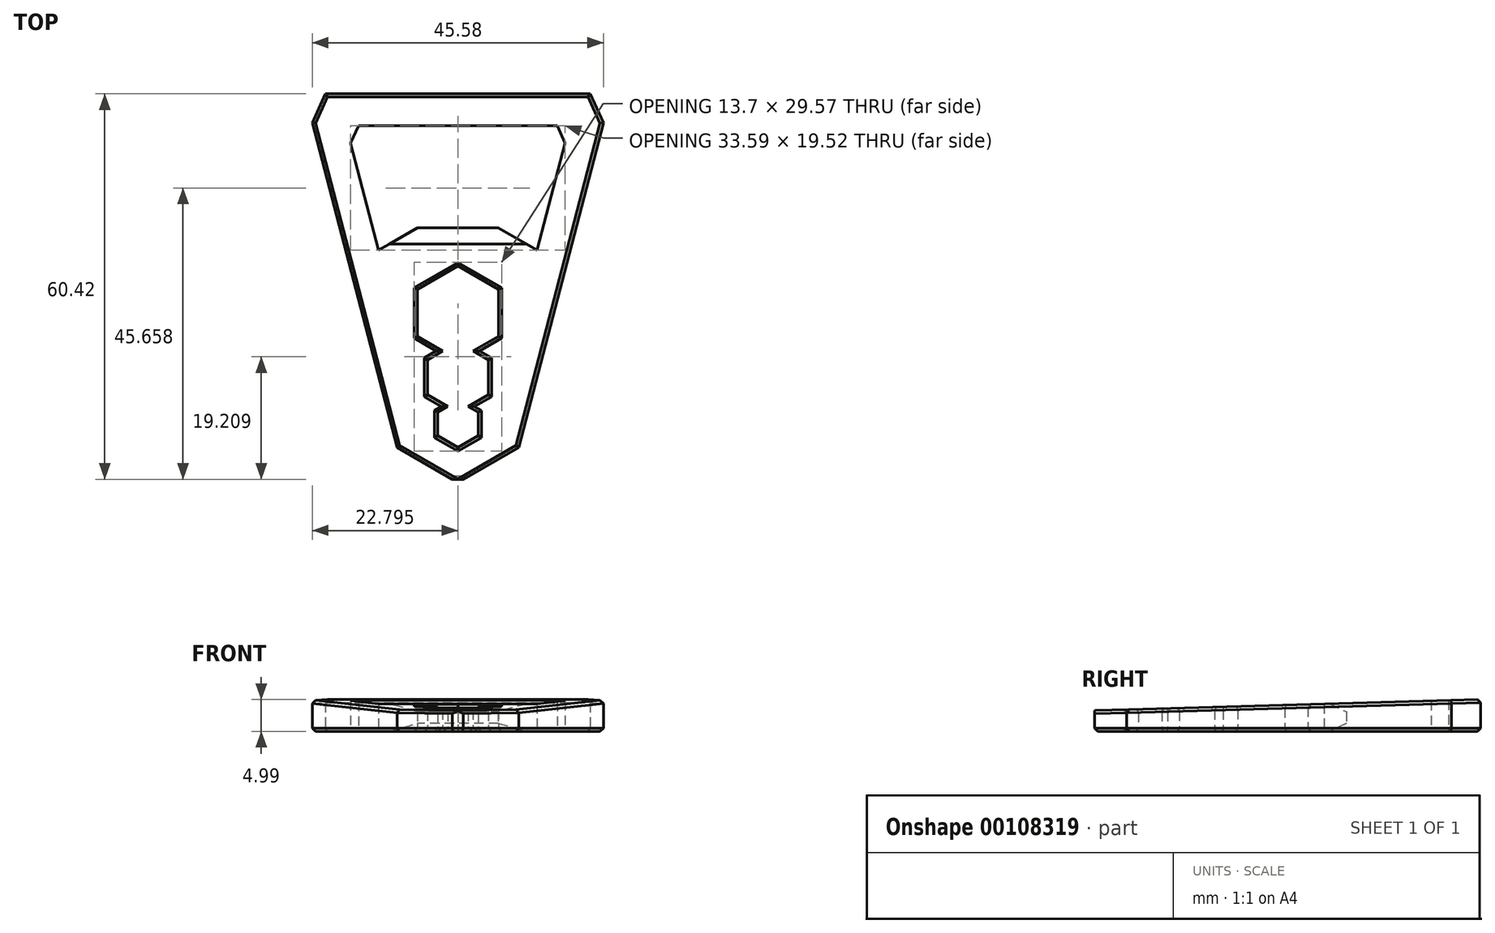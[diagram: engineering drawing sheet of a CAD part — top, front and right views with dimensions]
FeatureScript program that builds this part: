
annotation { "Feature Type Name" : "Feature", "Feature Type Description" : "" }
export const myFeature = defineFeature(function(context is Context, id is Id, definition is map)
    precondition{}
    {
        {
            var Q0;
            Q0=qCreatedBy(makeId("Top.planeOp"),FACE);
            var sketch = newSketch(context, id + "F0", { "sketchPlane" : qUnion([Q0])});
            skLineSegment(sketch, "E0", {"start": v(-34.12, -3.9) * mm, "end": v(-47.38, 46.95) * mm});
            skLineSegment(sketch, "E1", {"start": v(-47.38, 46.95) * mm, "end": v(-45.33, 51.5) * mm});
            skLineSegment(sketch, "E2", {"start": v(-45.33, 51.5) * mm, "end": v(-3.84, 51.5) * mm});
            skLineSegment(sketch, "E3", {"start": v(-3.84, 51.5) * mm, "end": v(-1.8, 46.95) * mm});
            skLineSegment(sketch, "E4", {"start": v(-1.8, 46.95) * mm, "end": v(-15.05, -3.9) * mm});
            skLineSegment(sketch, "E5", {"start": v(-23.71, -8.9) * mm, "end": v(-25.46, -8.9) * mm});
            skLineSegment(sketch, "E6", {"start": v(-24.59, -8.9) * mm, "end": v(-24.59, 51.5) * mm, "construction": true});
            skLineSegment(sketch, "E7", {"start": v(-15.05, -3.9) * mm, "end": v(-34.12, -3.9) * mm, "construction": true});
            skLineSegment(sketch, "E8", {"start": v(-1.8, 46.95) * mm, "end": v(-47.38, 46.95) * mm, "construction": true});
            skPoint(sketch, "E9", {"position": v(-24.59, 46.95) * mm});
            skPoint(sketch, "E10", {"position": v(-24.59, -3.9) * mm});
            skCircle(sketch, "E11.cCircle", {"center": v(-24.59, -0.24) * mm, "radius": 3.18 * mm, "construction": true});
            skLineSegment(sketch, "E11.0", {"start": v(-24.59, 3.43) * mm, "end": v(-21.41, 1.6) * mm, "construction": true});
            skLineSegment(sketch, "E11.1", {"start": v(-21.41, 1.6) * mm, "end": v(-21.41, -2.07) * mm, "construction": true});
            skLineSegment(sketch, "E11.2", {"start": v(-21.41, -2.07) * mm, "end": v(-24.59, -3.9) * mm, "construction": true});
            skLineSegment(sketch, "E11.3", {"start": v(-24.59, -3.9) * mm, "end": v(-27.76, -2.07) * mm, "construction": true});
            skLineSegment(sketch, "E11.4", {"start": v(-27.76, -2.07) * mm, "end": v(-27.76, 1.6) * mm, "construction": true});
            skLineSegment(sketch, "E11.5", {"start": v(-27.76, 1.6) * mm, "end": v(-24.59, 3.43) * mm, "construction": true});
            skPoint(sketch, "E11.0.midPoint", {"position": v(-23, 2.5) * mm});
            skCircle(sketch, "E12.cCircle", {"center": v(-24.59, 7.1) * mm, "radius": 4.76 * mm, "construction": true});
            skLineSegment(sketch, "E12.0", {"start": v(-29.35, 4.34) * mm, "end": v(-29.35, 9.84) * mm, "construction": true});
            skLineSegment(sketch, "E12.1", {"start": v(-29.35, 9.84) * mm, "end": v(-24.59, 12.6) * mm, "construction": true});
            skLineSegment(sketch, "E12.2", {"start": v(-24.59, 12.6) * mm, "end": v(-19.82, 9.84) * mm, "construction": true});
            skLineSegment(sketch, "E12.3", {"start": v(-19.82, 9.84) * mm, "end": v(-19.82, 4.34) * mm, "construction": true});
            skLineSegment(sketch, "E12.4", {"start": v(-19.82, 4.34) * mm, "end": v(-24.59, 1.6) * mm, "construction": true});
            skLineSegment(sketch, "E12.5", {"start": v(-24.59, 1.6) * mm, "end": v(-29.35, 4.34) * mm, "construction": true});
            skPoint(sketch, "E12.0.midPoint", {"position": v(-29.35, 7.1) * mm});
            skCircle(sketch, "E13.cCircle", {"center": v(-24.59, 17.17) * mm, "radius": 6.35 * mm, "construction": true});
            skLineSegment(sketch, "E13.0", {"start": v(-30.94, 13.5) * mm, "end": v(-30.94, 20.84) * mm, "construction": true});
            skLineSegment(sketch, "E13.1", {"start": v(-30.94, 20.84) * mm, "end": v(-24.59, 24.5) * mm, "construction": true});
            skLineSegment(sketch, "E13.2", {"start": v(-24.59, 24.5) * mm, "end": v(-18.24, 20.84) * mm, "construction": true});
            skLineSegment(sketch, "E13.3", {"start": v(-18.24, 20.84) * mm, "end": v(-18.24, 13.5) * mm, "construction": true});
            skLineSegment(sketch, "E13.4", {"start": v(-18.24, 13.5) * mm, "end": v(-24.59, 9.84) * mm, "construction": true});
            skLineSegment(sketch, "E13.5", {"start": v(-24.59, 9.84) * mm, "end": v(-30.94, 13.5) * mm, "construction": true});
            skPoint(sketch, "E13.0.midPoint", {"position": v(-30.94, 17.17) * mm});
            skLineSegment(sketch, "E14", {"start": v(-38.21, 43.5) * mm, "end": v(-10.96, 43.5) * mm, "construction": true});
            skLineSegment(sketch, "E15", {"start": v(-10.96, 43.5) * mm, "end": v(-13.57, 33.5) * mm, "construction": true});
            skLineSegment(sketch, "E16", {"start": v(-13.57, 33.5) * mm, "end": v(-35.6, 33.5) * mm, "construction": true});
            skLineSegment(sketch, "E17", {"start": v(-35.6, 33.5) * mm, "end": v(-38.21, 43.5) * mm, "construction": true});
            skPoint(sketch, "E18", {"position": v(-24.59, 43.5) * mm});
            skPoint(sketch, "E19", {"position": v(-24.59, 33.5) * mm});
            skLineSegment(sketch, "E20", {"start": v(-42.1, 46.5) * mm, "end": v(-7.08, 46.5) * mm, "construction": true});
            skLineSegment(sketch, "E21", {"start": v(-7.08, 46.5) * mm, "end": v(-11.25, 30.5) * mm, "construction": true});
            skLineSegment(sketch, "E22", {"start": v(-18.25, 30.5) * mm, "end": v(-30.92, 30.5) * mm, "construction": true});
            skLineSegment(sketch, "E23", {"start": v(-37.92, 30.5) * mm, "end": v(-42.1, 46.5) * mm, "construction": true});
            skLineSegment(sketch, "E24", {"start": v(-36.9, 38.5) * mm, "end": v(-39.81, 37.75) * mm, "construction": true});
            skLineSegment(sketch, "E25", {"start": v(-12.26, 38.5) * mm, "end": v(-9.36, 37.75) * mm, "construction": true});
            skLineSegment(sketch, "E26", {"start": v(-24.59, 46.5) * mm, "end": v(-24.59, 43.5) * mm, "construction": true});
            skLineSegment(sketch, "E27", {"start": v(-24.59, 33.5) * mm, "end": v(-24.59, 30.5) * mm, "construction": true});
            skLineSegment(sketch, "E28", {"start": v(-7.08, 46.5) * mm, "end": v(-7.08, 51.5) * mm, "construction": true});
            skLineSegment(sketch, "E29", {"start": v(-7.08, 46.5) * mm, "end": v(-2.24, 45.24) * mm, "construction": true});
            skPoint(sketch, "E30", {"position": v(-22.2, 11.22) * mm});
            skLineSegment(sketch, "E31", {"start": v(-30.92, 30.5) * mm, "end": v(-37, 26.99) * mm, "construction": true});
            skLineSegment(sketch, "E32", {"start": v(-18.25, 30.5) * mm, "end": v(-12.16, 26.99) * mm, "construction": true});
            skLineSegment(sketch, "E33", {"start": v(-37.92, 30.5) * mm, "end": v(-37, 26.99) * mm, "construction": true});
            skLineSegment(sketch, "E34", {"start": v(-11.25, 30.5) * mm, "end": v(-12.16, 26.99) * mm, "construction": true});
            skLineSegment(sketch, "E35", {"start": v(-7.08, 46.5) * mm, "end": v(-2.52, 48.56) * mm, "construction": true});
            skLineSegment(sketch, "E36", {"start": v(-15.05, -3.9) * mm, "end": v(-23.71, -8.9) * mm});
            skLineSegment(sketch, "E37", {"start": v(-25.46, -8.9) * mm, "end": v(-34.12, -3.9) * mm});
            skLineSegment(sketch, "E38", {"start": v(-24.59, -3.9) * mm, "end": v(-21.41, -2.07) * mm});
            skLineSegment(sketch, "E39", {"start": v(-21.41, 1.6) * mm, "end": v(-23, 2.5) * mm});
            skLineSegment(sketch, "E40", {"start": v(-19.82, 4.34) * mm, "end": v(-19.82, 9.84) * mm});
            skLineSegment(sketch, "E41", {"start": v(-22.2, 11.22) * mm, "end": v(-18.24, 13.5) * mm});
            skLineSegment(sketch, "E42", {"start": v(-18.24, 20.84) * mm, "end": v(-24.59, 24.5) * mm});
            skLineSegment(sketch, "E43", {"start": v(-30.94, 20.84) * mm, "end": v(-30.94, 13.5) * mm});
            skLineSegment(sketch, "E44", {"start": v(-26.97, 11.22) * mm, "end": v(-29.35, 9.84) * mm});
            skLineSegment(sketch, "E45", {"start": v(-29.35, 4.34) * mm, "end": v(-26.17, 2.5) * mm});
            skLineSegment(sketch, "E46", {"start": v(-26.17, 2.5) * mm, "end": v(-27.76, 1.6) * mm});
            skLineSegment(sketch, "E47", {"start": v(-27.76, -2.07) * mm, "end": v(-24.59, -3.9) * mm});
            skLineSegment(sketch, "E48", {"start": v(-30.94, 20.84) * mm, "end": v(-24.59, 24.5) * mm});
            skLineSegment(sketch, "E49", {"start": v(-18.24, 13.5) * mm, "end": v(-18.24, 20.84) * mm});
            skLineSegment(sketch, "E50", {"start": v(-21.41, -2.07) * mm, "end": v(-21.41, 1.6) * mm});
            skLineSegment(sketch, "E51", {"start": v(-19.82, 4.34) * mm, "end": v(-23, 2.5) * mm});
            skLineSegment(sketch, "E52", {"start": v(-22.2, 11.22) * mm, "end": v(-19.82, 9.84) * mm});
            skLineSegment(sketch, "E53", {"start": v(-30.94, 13.5) * mm, "end": v(-26.97, 11.22) * mm});
            skLineSegment(sketch, "E54", {"start": v(-29.35, 9.84) * mm, "end": v(-29.35, 4.34) * mm});
            skLineSegment(sketch, "E55", {"start": v(-27.76, 1.6) * mm, "end": v(-27.76, -2.07) * mm});
            skLineSegment(sketch, "E56", {"start": v(-41.38, 43.77) * mm, "end": v(-40.15, 46.5) * mm});
            skLineSegment(sketch, "E57", {"start": v(-40.15, 46.5) * mm, "end": v(-9.02, 46.5) * mm});
            skLineSegment(sketch, "E58", {"start": v(-9.02, 46.5) * mm, "end": v(-7.8, 43.77) * mm});
            skLineSegment(sketch, "E59", {"start": v(-7.8, 43.77) * mm, "end": v(-12.16, 26.99) * mm});
            skLineSegment(sketch, "E60", {"start": v(-18.25, 30.5) * mm, "end": v(-30.92, 30.5) * mm});
            skLineSegment(sketch, "E61", {"start": v(-18.25, 30.5) * mm, "end": v(-12.16, 26.99) * mm});
            skLineSegment(sketch, "E62", {"start": v(-30.92, 30.5) * mm, "end": v(-37, 26.99) * mm});
            skLineSegment(sketch, "E63", {"start": v(-37, 26.99) * mm, "end": v(-41.38, 43.77) * mm});
            skLineSegment(sketch, "E64", {"start": v(-8.22, 44.74) * mm, "end": v(-10.96, 43.5) * mm, "construction": true});
            skLineSegment(sketch, "E65", {"start": v(-24.59, -3.9) * mm, "end": v(-24.59, -8.9) * mm});
            skSolve(sketch);
        }
        {
            var Q0;
            Q0 = qSketchRegion(id + "F0", true);
            extrude(context, id + "F1", {"entities" : qUnion([Q0]), "depth" : 5 * mm});
        }
        {
            var Q0;
            Q0=qCreatedBy(makeId("Right.planeOp"),FACE);
            var sketch = newSketch(context, id + "F2", { "sketchPlane" : qUnion([Q0])});
            skLineSegment(sketch, "E66", {"start": v(-8.9, 3.25) * mm, "end": v(51.5, 5) * mm});
            skLineSegment(sketch, "E67", {"start": v(-8.9, 3.25) * mm, "end": v(-8.9, 5) * mm});
            skLineSegment(sketch, "E68", {"start": v(-8.9, 5) * mm, "end": v(51.5, 5) * mm});
            skSolve(sketch);
        }
        {
            var Q0;
            Q0 = qSketchRegion(id + "F2", true);
            extrude(context, id + "F3", {"entities" : qUnion([Q0]), "operationType" : NewBodyOperationType.REMOVE, "endBound" : BoundingType.THROUGH_ALL, "oppositeDirection" : true, "depth" : 25 * mm});
        }
        {
            var Q0;
            Q0=makeQuery(id+"F1.opExtrude","CAP_EDGE",EDGE,{"disambiguationData":[OSD([sQuery(id+"F0.wireOp",EDGE,"E60")])],"isStart":false});
            var Q1;
            Q1=makeQuery(id+"F1.opExtrude","CAP_EDGE",EDGE,{"disambiguationData":[OSD([sQuery(id+"F0.wireOp",EDGE,"E60")])],"isStart":true});
            var Q2;
            Q2=makeQuery(id+"F3.boolean.opBoolean","INTERSECT",EDGE,{"derivedFrom":[makeQuery(id+"F1.opExtrude","SWEPT_FACE",FACE,{"disambiguationData":[OSD([sQuery(id+"F0.wireOp",EDGE,"E60")])]}),makeQuery(id+"F3.opExtrude","SWEPT_FACE",FACE,{"disambiguationData":[OSD([sQuery(id+"F2.wireOp",EDGE,"E66")])]})]});
            chamfer(context, id + "F4", {"entities" : qUnion([Q0, Q1, Q2]), "chamferType" : ChamferType.TWO_OFFSETS, "width1" : 1.25 * mm, "oppositeDirection" : false, "width2" : 2.5 * mm});
        }
        {
            var Q0;
            Q0=makeQuery(id+"F3.boolean.opBoolean","MERGE",EDGE,{"derivedFrom":[makeQuery(id+"F1.opExtrude","CAP_EDGE",EDGE,{"disambiguationData":[OSD([sQuery(id+"F0.wireOp",EDGE,"E2")])],"isStart":false}),makeQuery(id+"F3.opExtrude","SWEPT_EDGE",EDGE,{"disambiguationData":[OSD([sQuery(id+"F2.wireOp",EDGE,"E66"),sQuery(id+"F2.wireOp",EDGE,"E68")])]})]});
            var Q1;
            Q1=makeQuery(id+"F3.boolean.opBoolean","INTERSECT",EDGE,{"derivedFrom":[makeQuery(id+"F1.opExtrude","SWEPT_FACE",FACE,{"disambiguationData":[OSD([sQuery(id+"F0.wireOp",EDGE,"E1")])]}),makeQuery(id+"F3.opExtrude","SWEPT_FACE",FACE,{"disambiguationData":[OSD([sQuery(id+"F2.wireOp",EDGE,"E66")])]})]});
            var Q2;
            Q2=makeQuery(id+"F1.opExtrude","CAP_EDGE",EDGE,{"disambiguationData":[OSD([sQuery(id+"F0.wireOp",EDGE,"E1")])],"isStart":true});
            var Q3;
            Q3=makeQuery(id+"F1.opExtrude","CAP_EDGE",EDGE,{"disambiguationData":[OSD([sQuery(id+"F0.wireOp",EDGE,"E2")])],"isStart":true});
            var Q4;
            Q4=makeQuery(id+"F1.opExtrude","CAP_EDGE",EDGE,{"disambiguationData":[OSD([sQuery(id+"F0.wireOp",EDGE,"E3")])],"isStart":true});
            var Q5;
            Q5=makeQuery(id+"F3.boolean.opBoolean","INTERSECT",EDGE,{"derivedFrom":[makeQuery(id+"F1.opExtrude","SWEPT_FACE",FACE,{"disambiguationData":[OSD([sQuery(id+"F0.wireOp",EDGE,"E3")])]}),makeQuery(id+"F3.opExtrude","SWEPT_FACE",FACE,{"disambiguationData":[OSD([sQuery(id+"F2.wireOp",EDGE,"E66")])]})]});
            var Q6;
            Q6=makeQuery(id+"F3.boolean.opBoolean","INTERSECT",EDGE,{"derivedFrom":[makeQuery(id+"F1.opExtrude","SWEPT_FACE",FACE,{"disambiguationData":[OSD([sQuery(id+"F0.wireOp",EDGE,"E4")])]}),makeQuery(id+"F3.opExtrude","SWEPT_FACE",FACE,{"disambiguationData":[OSD([sQuery(id+"F2.wireOp",EDGE,"E66")])]})]});
            var Q7;
            Q7=makeQuery(id+"F1.opExtrude","CAP_EDGE",EDGE,{"disambiguationData":[OSD([sQuery(id+"F0.wireOp",EDGE,"E4")])],"isStart":true});
            var Q8;
            Q8=makeQuery(id+"F3.boolean.opBoolean","INTERSECT",EDGE,{"derivedFrom":[makeQuery(id+"F1.opExtrude","SWEPT_FACE",FACE,{"disambiguationData":[OSD([sQuery(id+"F0.wireOp",EDGE,"E36")])]}),makeQuery(id+"F3.opExtrude","SWEPT_FACE",FACE,{"disambiguationData":[OSD([sQuery(id+"F2.wireOp",EDGE,"E66")])]})]});
            var Q9;
            Q9=makeQuery(id+"F1.opExtrude","CAP_EDGE",EDGE,{"disambiguationData":[OSD([sQuery(id+"F0.wireOp",EDGE,"E36")])],"isStart":true});
            var Q10;
            Q10=makeQuery(id+"F3.boolean.opBoolean","COPY",EDGE,{"derivedFrom":makeQuery(id+"F3.opExtrude","SWEPT_EDGE",EDGE,{"disambiguationData":[OSD([sQuery(id+"F2.wireOp",EDGE,"E66"),sQuery(id+"F2.wireOp",EDGE,"E67")])]})});
            var Q11;
            Q11=makeQuery(id+"F1.opExtrude","CAP_EDGE",EDGE,{"disambiguationData":[OSD([sQuery(id+"F0.wireOp",EDGE,"E5")])],"isStart":true});
            var Q12;
            Q12=makeQuery(id+"F1.opExtrude","CAP_EDGE",EDGE,{"disambiguationData":[OSD([sQuery(id+"F0.wireOp",EDGE,"E37")])],"isStart":true});
            var Q13;
            Q13=makeQuery(id+"F3.boolean.opBoolean","INTERSECT",EDGE,{"derivedFrom":[makeQuery(id+"F1.opExtrude","SWEPT_FACE",FACE,{"disambiguationData":[OSD([sQuery(id+"F0.wireOp",EDGE,"E37")])]}),makeQuery(id+"F3.opExtrude","SWEPT_FACE",FACE,{"disambiguationData":[OSD([sQuery(id+"F2.wireOp",EDGE,"E66")])]})]});
            var Q14;
            Q14=makeQuery(id+"F3.boolean.opBoolean","INTERSECT",EDGE,{"derivedFrom":[makeQuery(id+"F1.opExtrude","SWEPT_FACE",FACE,{"disambiguationData":[OSD([sQuery(id+"F0.wireOp",EDGE,"E0")])]}),makeQuery(id+"F3.opExtrude","SWEPT_FACE",FACE,{"disambiguationData":[OSD([sQuery(id+"F2.wireOp",EDGE,"E66")])]})]});
            var Q15;
            Q15=makeQuery(id+"F1.opExtrude","CAP_EDGE",EDGE,{"disambiguationData":[OSD([sQuery(id+"F0.wireOp",EDGE,"E0")])],"isStart":true});
            var Q16;
            Q16=makeQuery(id+"F3.boolean.opBoolean","INTERSECT",EDGE,{"derivedFrom":[makeQuery(id+"F1.opExtrude","SWEPT_FACE",FACE,{"disambiguationData":[OSD([sQuery(id+"F0.wireOp",EDGE,"E49")])]}),makeQuery(id+"F3.opExtrude","SWEPT_FACE",FACE,{"disambiguationData":[OSD([sQuery(id+"F2.wireOp",EDGE,"E66")])]})]});
            var Q17;
            Q17=makeQuery(id+"F3.boolean.opBoolean","INTERSECT",EDGE,{"derivedFrom":[makeQuery(id+"F1.opExtrude","SWEPT_FACE",FACE,{"disambiguationData":[OSD([sQuery(id+"F0.wireOp",EDGE,"E42")])]}),makeQuery(id+"F3.opExtrude","SWEPT_FACE",FACE,{"disambiguationData":[OSD([sQuery(id+"F2.wireOp",EDGE,"E66")])]})]});
            var Q18;
            Q18=makeQuery(id+"F3.boolean.opBoolean","INTERSECT",EDGE,{"derivedFrom":[makeQuery(id+"F1.opExtrude","SWEPT_FACE",FACE,{"disambiguationData":[OSD([sQuery(id+"F0.wireOp",EDGE,"E48")])]}),makeQuery(id+"F3.opExtrude","SWEPT_FACE",FACE,{"disambiguationData":[OSD([sQuery(id+"F2.wireOp",EDGE,"E66")])]})]});
            var Q19;
            Q19=makeQuery(id+"F3.boolean.opBoolean","INTERSECT",EDGE,{"derivedFrom":[makeQuery(id+"F1.opExtrude","SWEPT_FACE",FACE,{"disambiguationData":[OSD([sQuery(id+"F0.wireOp",EDGE,"E43")])]}),makeQuery(id+"F3.opExtrude","SWEPT_FACE",FACE,{"disambiguationData":[OSD([sQuery(id+"F2.wireOp",EDGE,"E66")])]})]});
            var Q20;
            Q20=makeQuery(id+"F3.boolean.opBoolean","INTERSECT",EDGE,{"derivedFrom":[makeQuery(id+"F1.opExtrude","SWEPT_FACE",FACE,{"disambiguationData":[OSD([sQuery(id+"F0.wireOp",EDGE,"E53")])]}),makeQuery(id+"F3.opExtrude","SWEPT_FACE",FACE,{"disambiguationData":[OSD([sQuery(id+"F2.wireOp",EDGE,"E66")])]})]});
            var Q21;
            Q21=makeQuery(id+"F3.boolean.opBoolean","INTERSECT",EDGE,{"derivedFrom":[makeQuery(id+"F1.opExtrude","SWEPT_FACE",FACE,{"disambiguationData":[OSD([sQuery(id+"F0.wireOp",EDGE,"E41")])]}),makeQuery(id+"F3.opExtrude","SWEPT_FACE",FACE,{"disambiguationData":[OSD([sQuery(id+"F2.wireOp",EDGE,"E66")])]})]});
            var Q22;
            Q22=makeQuery(id+"F3.boolean.opBoolean","INTERSECT",EDGE,{"derivedFrom":[makeQuery(id+"F1.opExtrude","SWEPT_FACE",FACE,{"disambiguationData":[OSD([sQuery(id+"F0.wireOp",EDGE,"E52")])]}),makeQuery(id+"F3.opExtrude","SWEPT_FACE",FACE,{"disambiguationData":[OSD([sQuery(id+"F2.wireOp",EDGE,"E66")])]})]});
            var Q23;
            Q23=makeQuery(id+"F3.boolean.opBoolean","INTERSECT",EDGE,{"derivedFrom":[makeQuery(id+"F1.opExtrude","SWEPT_FACE",FACE,{"disambiguationData":[OSD([sQuery(id+"F0.wireOp",EDGE,"E40")])]}),makeQuery(id+"F3.opExtrude","SWEPT_FACE",FACE,{"disambiguationData":[OSD([sQuery(id+"F2.wireOp",EDGE,"E66")])]})]});
            var Q24;
            Q24=makeQuery(id+"F3.boolean.opBoolean","INTERSECT",EDGE,{"derivedFrom":[makeQuery(id+"F1.opExtrude","SWEPT_FACE",FACE,{"disambiguationData":[OSD([sQuery(id+"F0.wireOp",EDGE,"E51")])]}),makeQuery(id+"F3.opExtrude","SWEPT_FACE",FACE,{"disambiguationData":[OSD([sQuery(id+"F2.wireOp",EDGE,"E66")])]})]});
            var Q25;
            Q25=makeQuery(id+"F3.boolean.opBoolean","INTERSECT",EDGE,{"derivedFrom":[makeQuery(id+"F1.opExtrude","SWEPT_FACE",FACE,{"disambiguationData":[OSD([sQuery(id+"F0.wireOp",EDGE,"E39")])]}),makeQuery(id+"F3.opExtrude","SWEPT_FACE",FACE,{"disambiguationData":[OSD([sQuery(id+"F2.wireOp",EDGE,"E66")])]})]});
            var Q26;
            Q26=makeQuery(id+"F3.boolean.opBoolean","INTERSECT",EDGE,{"derivedFrom":[makeQuery(id+"F1.opExtrude","SWEPT_FACE",FACE,{"disambiguationData":[OSD([sQuery(id+"F0.wireOp",EDGE,"E50")])]}),makeQuery(id+"F3.opExtrude","SWEPT_FACE",FACE,{"disambiguationData":[OSD([sQuery(id+"F2.wireOp",EDGE,"E66")])]})]});
            var Q27;
            Q27=makeQuery(id+"F3.boolean.opBoolean","INTERSECT",EDGE,{"derivedFrom":[makeQuery(id+"F1.opExtrude","SWEPT_FACE",FACE,{"disambiguationData":[OSD([sQuery(id+"F0.wireOp",EDGE,"E38")])]}),makeQuery(id+"F3.opExtrude","SWEPT_FACE",FACE,{"disambiguationData":[OSD([sQuery(id+"F2.wireOp",EDGE,"E66")])]})]});
            var Q28;
            Q28=makeQuery(id+"F3.boolean.opBoolean","INTERSECT",EDGE,{"derivedFrom":[makeQuery(id+"F1.opExtrude","SWEPT_FACE",FACE,{"disambiguationData":[OSD([sQuery(id+"F0.wireOp",EDGE,"E47")])]}),makeQuery(id+"F3.opExtrude","SWEPT_FACE",FACE,{"disambiguationData":[OSD([sQuery(id+"F2.wireOp",EDGE,"E66")])]})]});
            var Q29;
            Q29=makeQuery(id+"F3.boolean.opBoolean","INTERSECT",EDGE,{"derivedFrom":[makeQuery(id+"F1.opExtrude","SWEPT_FACE",FACE,{"disambiguationData":[OSD([sQuery(id+"F0.wireOp",EDGE,"E55")])]}),makeQuery(id+"F3.opExtrude","SWEPT_FACE",FACE,{"disambiguationData":[OSD([sQuery(id+"F2.wireOp",EDGE,"E66")])]})]});
            var Q30;
            Q30=makeQuery(id+"F3.boolean.opBoolean","INTERSECT",EDGE,{"derivedFrom":[makeQuery(id+"F1.opExtrude","SWEPT_FACE",FACE,{"disambiguationData":[OSD([sQuery(id+"F0.wireOp",EDGE,"E46")])]}),makeQuery(id+"F3.opExtrude","SWEPT_FACE",FACE,{"disambiguationData":[OSD([sQuery(id+"F2.wireOp",EDGE,"E66")])]})]});
            var Q31;
            Q31=makeQuery(id+"F3.boolean.opBoolean","INTERSECT",EDGE,{"derivedFrom":[makeQuery(id+"F1.opExtrude","SWEPT_FACE",FACE,{"disambiguationData":[OSD([sQuery(id+"F0.wireOp",EDGE,"E45")])]}),makeQuery(id+"F3.opExtrude","SWEPT_FACE",FACE,{"disambiguationData":[OSD([sQuery(id+"F2.wireOp",EDGE,"E66")])]})]});
            var Q32;
            Q32=makeQuery(id+"F3.boolean.opBoolean","INTERSECT",EDGE,{"derivedFrom":[makeQuery(id+"F1.opExtrude","SWEPT_FACE",FACE,{"disambiguationData":[OSD([sQuery(id+"F0.wireOp",EDGE,"E54")])]}),makeQuery(id+"F3.opExtrude","SWEPT_FACE",FACE,{"disambiguationData":[OSD([sQuery(id+"F2.wireOp",EDGE,"E66")])]})]});
            var Q33;
            Q33=makeQuery(id+"F3.boolean.opBoolean","INTERSECT",EDGE,{"derivedFrom":[makeQuery(id+"F1.opExtrude","SWEPT_FACE",FACE,{"disambiguationData":[OSD([sQuery(id+"F0.wireOp",EDGE,"E44")])]}),makeQuery(id+"F3.opExtrude","SWEPT_FACE",FACE,{"disambiguationData":[OSD([sQuery(id+"F2.wireOp",EDGE,"E66")])]})]});
            var Q34;
            Q34=makeQuery(id+"F1.opExtrude","CAP_EDGE",EDGE,{"disambiguationData":[OSD([sQuery(id+"F0.wireOp",EDGE,"E55")])],"isStart":true});
            var Q35;
            Q35=makeQuery(id+"F1.opExtrude","CAP_EDGE",EDGE,{"disambiguationData":[OSD([sQuery(id+"F0.wireOp",EDGE,"E47")])],"isStart":true});
            var Q36;
            Q36=makeQuery(id+"F1.opExtrude","CAP_EDGE",EDGE,{"disambiguationData":[OSD([sQuery(id+"F0.wireOp",EDGE,"E38")])],"isStart":true});
            var Q37;
            Q37=makeQuery(id+"F1.opExtrude","CAP_EDGE",EDGE,{"disambiguationData":[OSD([sQuery(id+"F0.wireOp",EDGE,"E50")])],"isStart":true});
            var Q38;
            Q38=makeQuery(id+"F1.opExtrude","CAP_EDGE",EDGE,{"disambiguationData":[OSD([sQuery(id+"F0.wireOp",EDGE,"E39")])],"isStart":true});
            var Q39;
            Q39=makeQuery(id+"F1.opExtrude","CAP_EDGE",EDGE,{"disambiguationData":[OSD([sQuery(id+"F0.wireOp",EDGE,"E46")])],"isStart":true});
            var Q40;
            Q40=makeQuery(id+"F1.opExtrude","CAP_EDGE",EDGE,{"disambiguationData":[OSD([sQuery(id+"F0.wireOp",EDGE,"E45")])],"isStart":true});
            var Q41;
            Q41=makeQuery(id+"F1.opExtrude","CAP_EDGE",EDGE,{"disambiguationData":[OSD([sQuery(id+"F0.wireOp",EDGE,"E51")])],"isStart":true});
            var Q42;
            Q42=makeQuery(id+"F1.opExtrude","CAP_EDGE",EDGE,{"disambiguationData":[OSD([sQuery(id+"F0.wireOp",EDGE,"E40")])],"isStart":true});
            var Q43;
            Q43=makeQuery(id+"F1.opExtrude","CAP_EDGE",EDGE,{"disambiguationData":[OSD([sQuery(id+"F0.wireOp",EDGE,"E52")])],"isStart":true});
            var Q44;
            Q44=makeQuery(id+"F1.opExtrude","CAP_EDGE",EDGE,{"disambiguationData":[OSD([sQuery(id+"F0.wireOp",EDGE,"E44")])],"isStart":true});
            var Q45;
            Q45=makeQuery(id+"F1.opExtrude","CAP_EDGE",EDGE,{"disambiguationData":[OSD([sQuery(id+"F0.wireOp",EDGE,"E54")])],"isStart":true});
            var Q46;
            Q46=makeQuery(id+"F1.opExtrude","CAP_EDGE",EDGE,{"disambiguationData":[OSD([sQuery(id+"F0.wireOp",EDGE,"E43")])],"isStart":true});
            var Q47;
            Q47=makeQuery(id+"F1.opExtrude","CAP_EDGE",EDGE,{"disambiguationData":[OSD([sQuery(id+"F0.wireOp",EDGE,"E53")])],"isStart":true});
            var Q48;
            Q48=makeQuery(id+"F1.opExtrude","CAP_EDGE",EDGE,{"disambiguationData":[OSD([sQuery(id+"F0.wireOp",EDGE,"E48")])],"isStart":true});
            var Q49;
            Q49=makeQuery(id+"F1.opExtrude","CAP_EDGE",EDGE,{"disambiguationData":[OSD([sQuery(id+"F0.wireOp",EDGE,"E42")])],"isStart":true});
            var Q50;
            Q50=makeQuery(id+"F1.opExtrude","CAP_EDGE",EDGE,{"disambiguationData":[OSD([sQuery(id+"F0.wireOp",EDGE,"E49")])],"isStart":true});
            var Q51;
            Q51=makeQuery(id+"F1.opExtrude","CAP_EDGE",EDGE,{"disambiguationData":[OSD([sQuery(id+"F0.wireOp",EDGE,"E41")])],"isStart":true});
            chamfer(context, id + "F5", {"entities" : qUnion([Q0, Q1, Q2, Q3, Q4, Q5, Q6, Q7, Q8, Q9, Q10, Q11, Q12, Q13, Q14, Q15, Q16, Q17, Q18, Q19, Q20, Q21, Q22, Q23, Q24, Q25, Q26, Q27, Q28, Q29, Q30, Q31, Q32, Q33, Q34, Q35, Q36, Q37, Q38, Q39, Q40, Q41, Q42, Q43, Q44, Q45, Q46, Q47, Q48, Q49, Q50, Q51]), "width" : 0.5 * mm, "tangentPropagation" : true});
        }
    });
